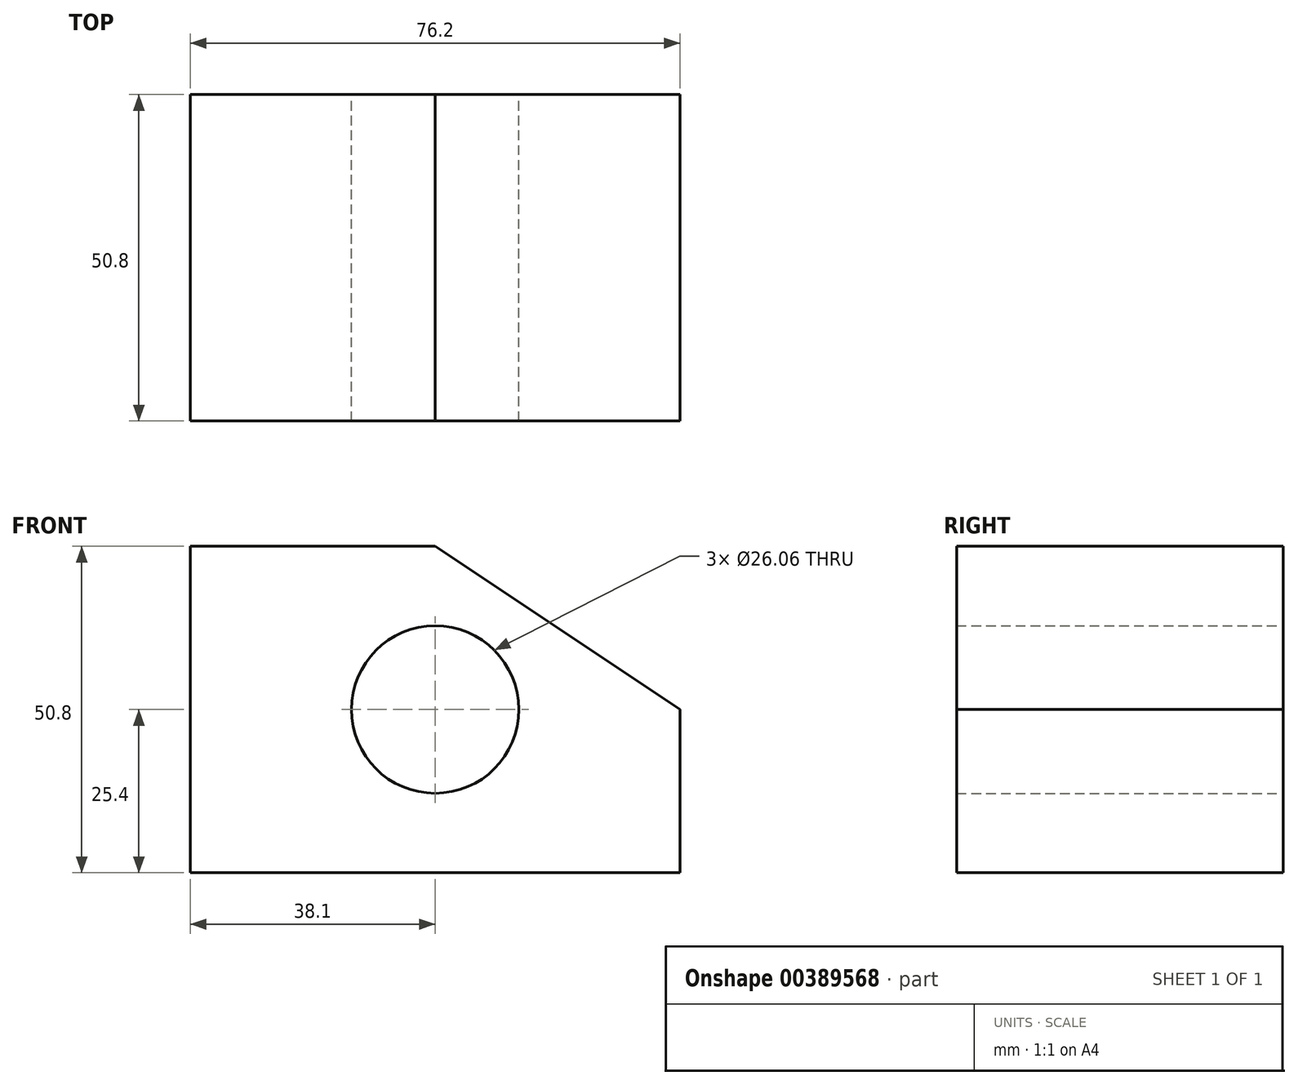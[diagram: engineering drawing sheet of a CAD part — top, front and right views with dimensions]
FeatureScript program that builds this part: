
annotation { "Feature Type Name" : "Feature", "Feature Type Description" : "" }
export const myFeature = defineFeature(function(context is Context, id is Id, definition is map)
    precondition{}
    {
        {
            var Q0;
            Q0=qCreatedBy(makeId("Front.planeOp"),FACE);
            var sketch = newSketch(context, id + "F0", { "sketchPlane" : qUnion([Q0])});
            skLineSegment(sketch, "E0", {"start": v(-38.1, 25.4) * mm, "end": v(-38.1, -25.4) * mm});
            skLineSegment(sketch, "E1", {"start": v(-38.1, -25.4) * mm, "end": v(38.1, -25.4) * mm});
            skLineSegment(sketch, "E2", {"start": v(38.1, -25.4) * mm, "end": v(38.1, 0) * mm});
            skLineSegment(sketch, "E3", {"start": v(-38.1, 25.4) * mm, "end": v(0, 25.4) * mm});
            skLineSegment(sketch, "E4", {"start": v(0, 25.4) * mm, "end": v(38.1, 0) * mm});
            skCircle(sketch, "E5", {"center": v(0, 0) * mm, "radius": 13.03 * mm});
            skSolve(sketch);
        }
        {
            var Q0;
            Q0=makeQuery(id+"F0.imprint","IMPRINT",FACE,{"disambiguationData":[TD([[makeQuery(id+"F0.imprint","IMPRINT",EDGE,{"derivedFrom":sQuery(id+"F0.wireOp",EDGE,"E0")}),1.0]])]});
            extrude(context, id + "F1", {"entities" : qUnion([Q0]), "depth" : 50.8 * mm});
        }
    });
